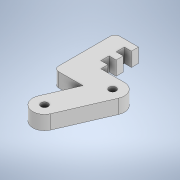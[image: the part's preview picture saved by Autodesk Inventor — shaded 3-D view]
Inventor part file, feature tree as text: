
AUTODESK INVENTOR PART (.ipt)
format: ipt  version: 2020 (Build 240168000, 168)  size: 159,744 bytes
history: native  units: mm
features: sketch x3, fillet x2, hole x2, other x1, extrude x1
ambient origin geometry x8: Origin, YZ Plane, XZ Plane, XY Plane, X Axis, Y Axis, Z Axis, Center Point
bodies: Body1 (feature_tree)
feature tree (9):
  other  "Bryła2"
  extrude  "Wyciągnięcie proste6"  Depth=6.0mm TaperAngle=0.0deg
  fillet  "Zaokrąglenie3"  Radius=2.0mm
  fillet  "Fillet4"  Radius=2.0mm
  hole  "Hole1"  [1 undecoded]
  hole  "Hole2"  [1 undecoded]
  sketch  "Szkic1"
  sketch  "Sketch8"  dims[d0=10.0mm d27=6.0mm d28=0.0mm d31=2.0mm d35=2.0mm]
  sketch  "Sketch9"  dims[d36=3.0mm d37=6.0mm d38=4.0mm d39=2.0mm d40=90.0deg d41=8.0mm d42=20.594885mm d43=3.0mm d44=6.0mm d45=4.0mm d46=2.0mm d47=90.0deg d48=8.0mm d49=20.594885mm d21=1.0mm d22=1.0mm d23=1.0mm d24=0.15mm d25=0.25mm d26=0.375mm d29=20.594885mm d30=0.0625mm d32=0.375mm]
note: 2 required parameter values undecoded (feature->parameter linkage not recoverable at this tier; creation-order binding heuristic only, values carry confidence <= 0.55)
